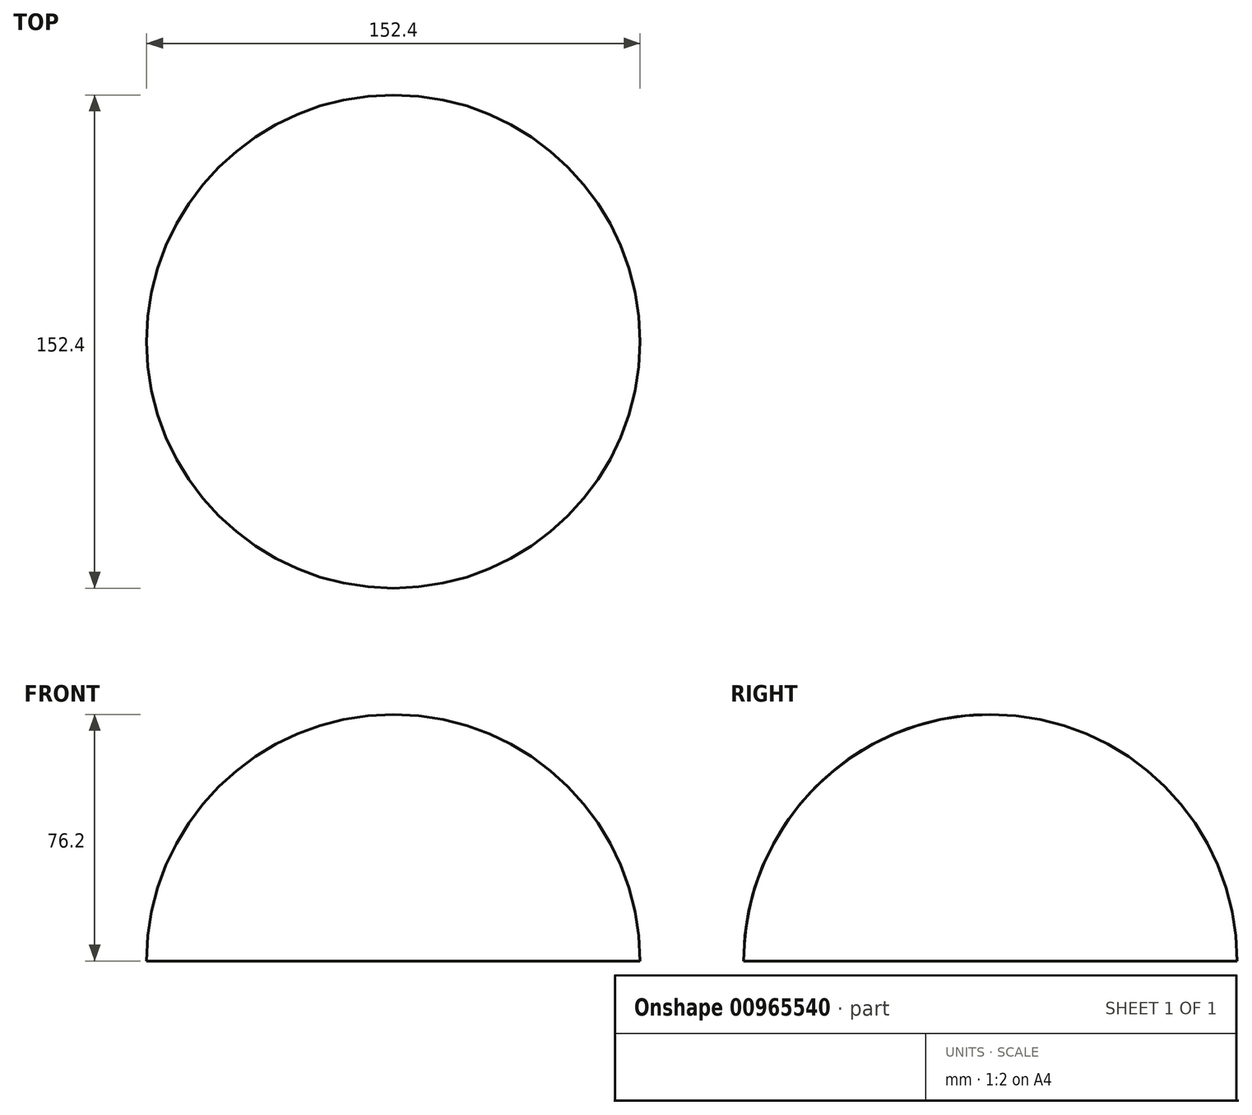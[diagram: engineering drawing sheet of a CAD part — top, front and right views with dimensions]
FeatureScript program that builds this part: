
annotation { "Feature Type Name" : "Feature", "Feature Type Description" : "" }
export const myFeature = defineFeature(function(context is Context, id is Id, definition is map)
    precondition{}
    {
        {
            var Q0;
            Q0=qCreatedBy(makeId("Right.planeOp"),FACE);
            var sketch = newSketch(context, id + "F0", { "sketchPlane" : qUnion([Q0])});
            skLineSegment(sketch, "E0", {"start": v(0, 0) * mm, "end": v(-76.2, 0) * mm});
            skLineSegment(sketch, "E1", {"start": v(0, 0) * mm, "end": v(0, 76.2) * mm});
            skArc(sketch, "E2", {"start": v(0, 76.2) * mm, "mid": v(-53.88, 53.88) * mm, "end": v(-76.2, 0) * mm});
            skSolve(sketch);
        }
        {
            var Q0;
            Q0=makeQuery(id+"F0.imprint","IMPRINT",FACE,{"disambiguationData":[TD([[makeQuery(id+"F0.imprint","IMPRINT",EDGE,{"derivedFrom":sQuery(id+"F0.wireOp",EDGE,"E0")}),-1.0]])]});
            var Q1;
            Q1=sQuery(id+"F0.wireOp",EDGE,"E1");
            revolve(context, id + "F1", {"surfaceOperationType" : NewSurfaceOperationType.NEW, "entities" : qUnion([Q0]), "axis" : qUnion([Q1]), "revolveType" : RevolveType.FULL});
        }
    });
